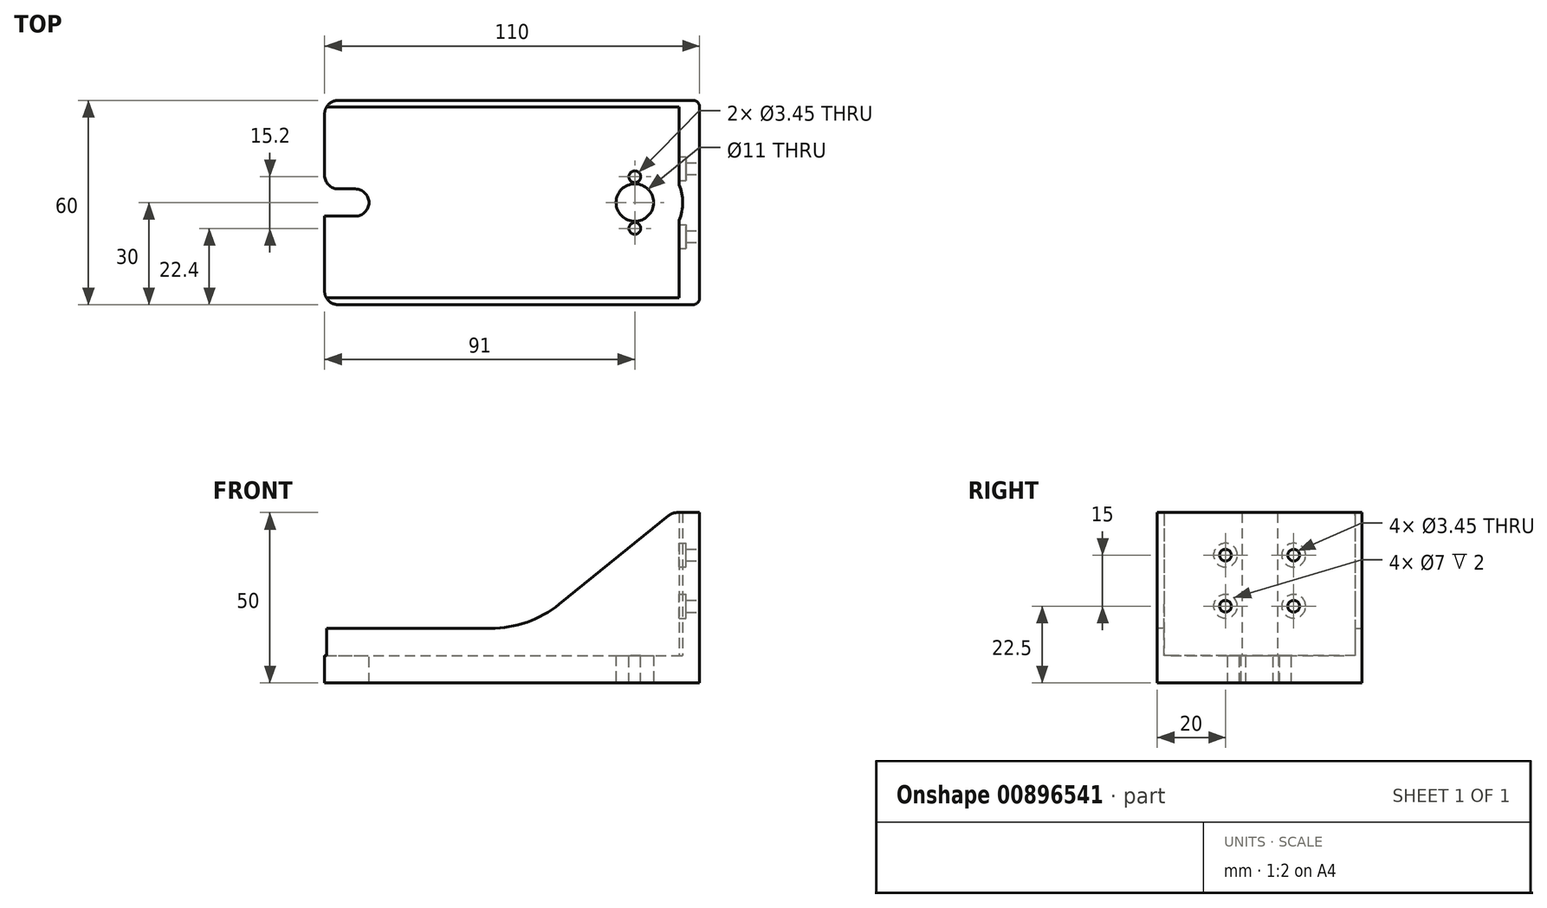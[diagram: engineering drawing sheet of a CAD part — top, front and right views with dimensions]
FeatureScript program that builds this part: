
annotation { "Feature Type Name" : "Feature", "Feature Type Description" : "" }
export const myFeature = defineFeature(function(context is Context, id is Id, definition is map)
    precondition{}
    {
        {
            var Q0;
            Q0=qCreatedBy(makeId("Top.planeOp"),FACE);
            var sketch = newSketch(context, id + "F0", { "sketchPlane" : qUnion([Q0])});
            skLineSegment(sketch, "E0.bottom", {"start": v(0, 0) * mm, "end": v(110, 0) * mm});
            skLineSegment(sketch, "E0.top", {"start": v(0, 60) * mm, "end": v(110, 60) * mm});
            skLineSegment(sketch, "E0.left", {"start": v(0, 0) * mm, "end": v(0, 60) * mm});
            skLineSegment(sketch, "E0.right", {"start": v(110, 0) * mm, "end": v(110, 60) * mm});
            skSolve(sketch);
        }
        {
            var Q0;
            Q0 = qSketchRegion(id + "F0", true);
            extrude(context, id + "F1", {"entities" : qUnion([Q0]), "depth" : 8 * mm, "offsetDistance" : 25 * mm});
        }
        {
            var Q0;
            Q0=makeQuery(id+"F1.opExtrude","SWEPT_FACE",FACE,{"disambiguationData":[OSD([sQuery(id+"F0.wireOp",EDGE,"E0.bottom")])]});
            var sketch = newSketch(context, id + "F2", { "sketchPlane" : qUnion([Q0])});
            skLineSegment(sketch, "E1", {"start": v(110, 8) * mm, "end": v(110, 50) * mm});
            skLineSegment(sketch, "E2", {"start": v(110, 50) * mm, "end": v(102, 50) * mm});
            skLineSegment(sketch, "E3", {"start": v(102, 50) * mm, "end": v(60, 16) * mm});
            skLineSegment(sketch, "E4", {"start": v(60, 16) * mm, "end": v(0, 16) * mm});
            skLineSegment(sketch, "E5", {"start": v(0, 16) * mm, "end": v(0, 8) * mm});
            skLineSegment(sketch, "E6", {"start": v(0, 8) * mm, "end": v(110, 8) * mm});
            skSolve(sketch);
        }
        {
            var Q0;
            Q0 = qSketchRegion(id + "F2", true);
            extrude(context, id + "F3", {"entities" : qUnion([Q0]), "operationType" : NewBodyOperationType.ADD, "oppositeDirection" : true, "depth" : 2 * mm, "offsetDistance" : 25 * mm});
        }
        {
            var Q0;
            Q0=makeQuery(id+"F1.opExtrude","SWEPT_FACE",FACE,{"disambiguationData":[OSD([sQuery(id+"F0.wireOp",EDGE,"E0.top")])]});
            var sketch = newSketch(context, id + "F4", { "sketchPlane" : qUnion([Q0])});
            skLineSegment(sketch, "E7", {"start": v(-110, 8) * mm, "end": v(-110, 50) * mm});
            skLineSegment(sketch, "E8", {"start": v(-110, 50) * mm, "end": v(-102, 50) * mm});
            skLineSegment(sketch, "E9", {"start": v(-102, 50) * mm, "end": v(-60, 16) * mm});
            skLineSegment(sketch, "E10", {"start": v(-60, 16) * mm, "end": v(0, 16) * mm});
            skLineSegment(sketch, "E11", {"start": v(0, 16) * mm, "end": v(0, 8) * mm});
            skLineSegment(sketch, "E12", {"start": v(0, 8) * mm, "end": v(-110, 8) * mm});
            skSolve(sketch);
        }
        {
            var Q0;
            Q0 = qSketchRegion(id + "F4", true);
            extrude(context, id + "F5", {"entities" : qUnion([Q0]), "operationType" : NewBodyOperationType.ADD, "oppositeDirection" : true, "depth" : 2 * mm, "offsetDistance" : 25 * mm});
        }
        {
            var Q0;
            Q0=makeQuery(id+"F1.opExtrude","CAP_FACE",FACE,{"disambiguationData":[OSD([sQuery(id+"F0.wireOp",EDGE,"E0.bottom"),sQuery(id+"F0.wireOp",EDGE,"E0.top"),sQuery(id+"F0.wireOp",EDGE,"E0.left"),sQuery(id+"F0.wireOp",EDGE,"E0.right")])],"isStart":false});
            var sketch = newSketch(context, id + "F6", { "sketchPlane" : qUnion([Q0])});
            skLineSegment(sketch, "E13.bottom", {"start": v(110, 58) * mm, "end": v(104, 58) * mm});
            skLineSegment(sketch, "E13.top", {"start": v(110, 2) * mm, "end": v(104, 2) * mm});
            skLineSegment(sketch, "E13.left", {"start": v(110, 58) * mm, "end": v(110, 2) * mm});
            skLineSegment(sketch, "E13.right", {"start": v(104, 58) * mm, "end": v(104, 2) * mm});
            skSolve(sketch);
        }
        {
            var Q0;
            Q0 = qSketchRegion(id + "F6", true);
            extrude(context, id + "F7", {"entities" : qUnion([Q0]), "operationType" : NewBodyOperationType.ADD, "depth" : 42 * mm, "offsetDistance" : 25 * mm});
        }
        {
            var Q0;
            Q0=makeQuery(id+"F1.opExtrude","CAP_FACE",FACE,{"disambiguationData":[OSD([sQuery(id+"F0.wireOp",EDGE,"E0.bottom"),sQuery(id+"F0.wireOp",EDGE,"E0.top"),sQuery(id+"F0.wireOp",EDGE,"E0.left"),sQuery(id+"F0.wireOp",EDGE,"E0.right")])],"isStart":false});
            var sketch = newSketch(context, id + "F8", { "sketchPlane" : qUnion([Q0])});
            skLineSegment(sketch, "E14.bottom", {"start": v(0, 34) * mm, "end": v(13, 34) * mm});
            skLineSegment(sketch, "E14.top", {"start": v(0, 26) * mm, "end": v(13, 26) * mm});
            skLineSegment(sketch, "E14.left", {"start": v(0, 34) * mm, "end": v(0, 26) * mm});
            skLineSegment(sketch, "E14.right", {"start": v(13, 34) * mm, "end": v(13, 26) * mm});
            skLineSegment(sketch, "E15", {"start": v(0, 30) * mm, "end": v(13, 30) * mm, "construction": true});
            skSolve(sketch);
        }
        {
            var Q0;
            Q0 = qSketchRegion(id + "F8", true);
            extrude(context, id + "F9", {"entities" : qUnion([Q0]), "operationType" : NewBodyOperationType.REMOVE, "oppositeDirection" : true, "depth" : 8 * mm, "offsetDistance" : 25 * mm});
        }
        {
            var Q0;
            Q0=makeQuery(id+"F5.opExtrude","SWEPT_EDGE",EDGE,{"disambiguationData":[OSD([sQuery(id+"F4.wireOp",EDGE,"E8"),sQuery(id+"F4.wireOp",EDGE,"E9")])]});
            var Q1;
            Q1=makeQuery(id+"F3.opExtrude","SWEPT_EDGE",EDGE,{"disambiguationData":[OSD([sQuery(id+"F2.wireOp",EDGE,"E2"),sQuery(id+"F2.wireOp",EDGE,"E3")])]});
            var Q2;
            Q2=makeQuery(id+"F5.boolean.opBoolean","MERGE",EDGE,{"derivedFrom":[makeQuery(id+"F1.opExtrude","SWEPT_EDGE",EDGE,{"disambiguationData":[OSD([sQuery(id+"F0.wireOp",EDGE,"E0.top"),sQuery(id+"F0.wireOp",EDGE,"E0.left")])]}),makeQuery(id+"F5.opExtrude","CAP_EDGE",EDGE,{"disambiguationData":[OSD([sQuery(id+"F4.wireOp",EDGE,"E11")])],"isStart":true})]});
            var Q3;
            Q3=makeQuery(id+"F9.boolean.opBoolean","COPY",EDGE,{"derivedFrom":makeQuery(id+"F9.opExtrude","SWEPT_EDGE",EDGE,{"disambiguationData":[OSD([sQuery(id+"F0.wireOp",EDGE,"E0.left"),sQuery(id+"F8.wireOp",EDGE,"E14.bottom"),sQuery(id+"F8.wireOp",EDGE,"E14.left")])]})});
            var Q4;
            Q4=makeQuery(id+"F9.boolean.opBoolean","COPY",EDGE,{"derivedFrom":makeQuery(id+"F9.opExtrude","SWEPT_EDGE",EDGE,{"disambiguationData":[OSD([sQuery(id+"F0.wireOp",EDGE,"E0.left"),sQuery(id+"F8.wireOp",EDGE,"E14.top"),sQuery(id+"F8.wireOp",EDGE,"E14.left")])]})});
            var Q5;
            Q5=makeQuery(id+"F9.boolean.opBoolean","COPY",EDGE,{"derivedFrom":makeQuery(id+"F9.opExtrude","SWEPT_EDGE",EDGE,{"disambiguationData":[OSD([sQuery(id+"F8.wireOp",EDGE,"E14.top"),sQuery(id+"F8.wireOp",EDGE,"E14.right")])]})});
            var Q6;
            Q6=makeQuery(id+"F9.boolean.opBoolean","COPY",EDGE,{"derivedFrom":makeQuery(id+"F9.opExtrude","SWEPT_EDGE",EDGE,{"disambiguationData":[OSD([sQuery(id+"F8.wireOp",EDGE,"E14.bottom"),sQuery(id+"F8.wireOp",EDGE,"E14.right")])]})});
            var Q7;
            Q7=makeQuery(id+"F3.boolean.opBoolean","MERGE",EDGE,{"derivedFrom":[makeQuery(id+"F1.opExtrude","SWEPT_EDGE",EDGE,{"disambiguationData":[OSD([sQuery(id+"F0.wireOp",EDGE,"E0.bottom"),sQuery(id+"F0.wireOp",EDGE,"E0.left")])]}),makeQuery(id+"F3.opExtrude","CAP_EDGE",EDGE,{"disambiguationData":[OSD([sQuery(id+"F2.wireOp",EDGE,"E5")])],"isStart":true})]});
            fillet(context, id + "F10", {"entities" : qUnion([Q0, Q1, Q2, Q3, Q4, Q5, Q6, Q7]), "radius" : 4 * mm, "tangentPropagation" : true, "defaultsChanged" : false, "vertexSettings" : [], "allowEdgeOverflow" : false});
        }
        {
            var Q0;
            Q0=makeQuery(id+"F5.opExtrude","CAP_EDGE",EDGE,{"disambiguationData":[OSD([sQuery(id+"F4.wireOp",EDGE,"E12")])],"isStart":false});
            var Q1;
            Q1=makeQuery(id+"F3.opExtrude","CAP_EDGE",EDGE,{"disambiguationData":[OSD([sQuery(id+"F2.wireOp",EDGE,"E6")])],"isStart":false});
            var Q2;
            Q2=makeQuery(id+"F3.opExtrude","SWEPT_EDGE",EDGE,{"disambiguationData":[OSD([sQuery(id+"F2.wireOp",EDGE,"E2"),sQuery(id+"F2.wireOp",EDGE,"E3")])]});
            var Q3;
            Q3=makeQuery(id+"F5.opExtrude","SWEPT_EDGE",EDGE,{"disambiguationData":[OSD([sQuery(id+"F4.wireOp",EDGE,"E8"),sQuery(id+"F4.wireOp",EDGE,"E9")])]});
            var Q4;
            Q4=makeQuery(id+"F3.boolean.opBoolean","MERGE",EDGE,{"derivedFrom":[makeQuery(id+"F1.opExtrude","SWEPT_EDGE",EDGE,{"disambiguationData":[OSD([sQuery(id+"F0.wireOp",EDGE,"E0.bottom"),sQuery(id+"F0.wireOp",EDGE,"E0.right")])]}),makeQuery(id+"F3.opExtrude","CAP_EDGE",EDGE,{"disambiguationData":[OSD([sQuery(id+"F2.wireOp",EDGE,"E1")])],"isStart":true})]});
            var Q5;
            Q5=makeQuery(id+"F5.boolean.opBoolean","MERGE",EDGE,{"derivedFrom":[makeQuery(id+"F1.opExtrude","SWEPT_EDGE",EDGE,{"disambiguationData":[OSD([sQuery(id+"F0.wireOp",EDGE,"E0.top"),sQuery(id+"F0.wireOp",EDGE,"E0.right")])]}),makeQuery(id+"F5.opExtrude","CAP_EDGE",EDGE,{"disambiguationData":[OSD([sQuery(id+"F4.wireOp",EDGE,"E7")])],"isStart":true})]});
            var Q6;
            Q6=makeQuery(id+"F7.opExtrude","SWEPT_EDGE",EDGE,{"disambiguationData":[OSD([sQuery(id+"F2.wireOp",EDGE,"E6"),sQuery(id+"F6.wireOp",EDGE,"E13.top"),sQuery(id+"F6.wireOp",EDGE,"E13.right")])]});
            var Q7;
            Q7=makeQuery(id+"F7.opExtrude","SWEPT_EDGE",EDGE,{"disambiguationData":[OSD([sQuery(id+"F4.wireOp",EDGE,"E12"),sQuery(id+"F6.wireOp",EDGE,"E13.bottom"),sQuery(id+"F6.wireOp",EDGE,"E13.right")])]});
            var Q8;
            Q8=makeQuery(id+"F7.opExtrude","CAP_EDGE",EDGE,{"disambiguationData":[OSD([sQuery(id+"F6.wireOp",EDGE,"E13.right")])],"isStart":true});
            fillet(context, id + "F11", {"entities" : qUnion([Q0, Q1, Q2, Q3, Q4, Q5, Q6, Q7, Q8]), "radius" : 2 * mm, "tangentPropagation" : true, "defaultsChanged" : true, "vertexSettings" : [], "allowEdgeOverflow" : false});
        }
        {
            var Q0;
            Q0=makeQuery(id+"F7.boolean.opBoolean","MERGE",FACE,{"derivedFrom":[makeQuery(id+"F5.boolean.opBoolean","MERGE",FACE,{"derivedFrom":[makeQuery(id+"F3.boolean.opBoolean","MERGE",FACE,{"derivedFrom":[makeQuery(id+"F1.opExtrude","SWEPT_FACE",FACE,{"disambiguationData":[OSD([sQuery(id+"F0.wireOp",EDGE,"E0.right")])]}),makeQuery(id+"F3.opExtrude","SWEPT_FACE",FACE,{"disambiguationData":[OSD([sQuery(id+"F2.wireOp",EDGE,"E1")])]})]}),makeQuery(id+"F5.opExtrude","SWEPT_FACE",FACE,{"disambiguationData":[OSD([sQuery(id+"F4.wireOp",EDGE,"E7")])]})]}),makeQuery(id+"F7.opExtrude","SWEPT_FACE",FACE,{"disambiguationData":[OSD([sQuery(id+"F6.wireOp",EDGE,"E13.left")])]})]});
            var sketch = newSketch(context, id + "F12", { "sketchPlane" : qUnion([Q0])});
            skLineSegment(sketch, "E16", {"start": v(30, 0) * mm, "end": v(30, 30) * mm, "construction": true});
            skLineSegment(sketch, "E17.bottom", {"start": v(20, 37.5) * mm, "end": v(40, 37.5) * mm, "construction": true});
            skLineSegment(sketch, "E17.top", {"start": v(20, 22.5) * mm, "end": v(40, 22.5) * mm, "construction": true});
            skLineSegment(sketch, "E17.left", {"start": v(20, 37.5) * mm, "end": v(20, 22.5) * mm, "construction": true});
            skLineSegment(sketch, "E17.right", {"start": v(40, 37.5) * mm, "end": v(40, 22.5) * mm, "construction": true});
            skLineSegment(sketch, "E18", {"start": v(30, 30) * mm, "end": v(30, 37.5) * mm, "construction": true});
            skLineSegment(sketch, "E19", {"start": v(30, 30) * mm, "end": v(20, 30) * mm, "construction": true});
            skCircle(sketch, "E20", {"center": v(20, 37.5) * mm, "radius": 1.73 * mm});
            skCircle(sketch, "E21", {"center": v(40, 37.5) * mm, "radius": 1.73 * mm});
            skCircle(sketch, "E22", {"center": v(40, 22.5) * mm, "radius": 1.73 * mm});
            skCircle(sketch, "E23", {"center": v(20, 22.5) * mm, "radius": 1.73 * mm});
            skCircle(sketch, "E24", {"center": v(20, 22.5) * mm, "radius": 3.5 * mm});
            skCircle(sketch, "E25", {"center": v(40, 22.5) * mm, "radius": 3.5 * mm});
            skCircle(sketch, "E26", {"center": v(40, 37.5) * mm, "radius": 3.5 * mm});
            skCircle(sketch, "E27", {"center": v(20, 37.5) * mm, "radius": 3.5 * mm});
            skSolve(sketch);
        }
        {
            var Q0;
            Q0=makeQuery(id+"F12.imprint","IMPRINT",FACE,{"disambiguationData":[TD([[makeQuery(id+"F12.imprint","IMPRINT",EDGE,{"derivedFrom":sQuery(id+"F12.wireOp",EDGE,"E20")}),1.0]])]});
            var Q1;
            Q1=makeQuery(id+"F12.imprint","IMPRINT",FACE,{"disambiguationData":[TD([[makeQuery(id+"F12.imprint","IMPRINT",EDGE,{"derivedFrom":sQuery(id+"F12.wireOp",EDGE,"E22")}),1.0]])]});
            var Q2;
            Q2=makeQuery(id+"F12.imprint","IMPRINT",FACE,{"disambiguationData":[TD([[makeQuery(id+"F12.imprint","IMPRINT",EDGE,{"derivedFrom":sQuery(id+"F12.wireOp",EDGE,"E23")}),1.0]])]});
            var Q3;
            Q3=makeQuery(id+"F12.imprint","IMPRINT",FACE,{"disambiguationData":[TD([[makeQuery(id+"F12.imprint","IMPRINT",EDGE,{"derivedFrom":sQuery(id+"F12.wireOp",EDGE,"E21")}),1.0]])]});
            extrude(context, id + "F13", {"entities" : qUnion([Q0, Q1, Q2, Q3]), "operationType" : NewBodyOperationType.REMOVE, "oppositeDirection" : true, "depth" : 6 * mm, "offsetDistance" : 25 * mm});
        }
        {
            var Q0;
            Q0 = qSketchRegion(id + "F12", true);
            extrude(context, id + "F14", {"entities" : qUnion([Q0]), "oppositeDirection" : true, "depth" : 3 * mm, "offsetDistance" : 25 * mm});
        }
        {
            var Q0;
            Q0=makeQuery(id+"F14.opExtrude","SWEPT_BODY",BODY,{"disambiguationData":[OSD([sQuery(id+"F12.wireOp",EDGE,"E20"),sQuery(id+"F12.wireOp",EDGE,"E27")])]});
            var Q1;
            Q1=makeQuery(id+"F14.opExtrude","SWEPT_BODY",BODY,{"disambiguationData":[OSD([sQuery(id+"F12.wireOp",EDGE,"E21"),sQuery(id+"F12.wireOp",EDGE,"E26")])]});
            var Q2;
            Q2=makeQuery(id+"F14.opExtrude","SWEPT_BODY",BODY,{"disambiguationData":[OSD([sQuery(id+"F12.wireOp",EDGE,"E22"),sQuery(id+"F12.wireOp",EDGE,"E25")])]});
            var Q3;
            Q3=makeQuery(id+"F14.opExtrude","SWEPT_BODY",BODY,{"disambiguationData":[OSD([sQuery(id+"F12.wireOp",EDGE,"E23"),sQuery(id+"F12.wireOp",EDGE,"E24")])]});
            transform(context, id + "F15", {"entities" : qUnion([Q0, Q1, Q2, Q3]), "transformType" : TransformType.TRANSLATION_3D, "dx" : -4 * mm, "dy" : 0 * mm, "dz" : 0 * mm, "makeCopy" : false});
        }
        {
            var Q0;
            Q0=makeQuery(id+"F14.opExtrude","SWEPT_BODY",BODY,{"disambiguationData":[OSD([sQuery(id+"F12.wireOp",EDGE,"E20"),sQuery(id+"F12.wireOp",EDGE,"E27")])]});
            var Q1;
            Q1=makeQuery(id+"F14.opExtrude","SWEPT_BODY",BODY,{"disambiguationData":[OSD([sQuery(id+"F12.wireOp",EDGE,"E21"),sQuery(id+"F12.wireOp",EDGE,"E26")])]});
            var Q2;
            Q2=makeQuery(id+"F14.opExtrude","SWEPT_BODY",BODY,{"disambiguationData":[OSD([sQuery(id+"F12.wireOp",EDGE,"E22"),sQuery(id+"F12.wireOp",EDGE,"E25")])]});
            var Q3;
            Q3=makeQuery(id+"F14.opExtrude","SWEPT_BODY",BODY,{"disambiguationData":[OSD([sQuery(id+"F12.wireOp",EDGE,"E23"),sQuery(id+"F12.wireOp",EDGE,"E24")])]});
            var Q4;
            Q4=makeQuery(id+"F1.opExtrude","SWEPT_BODY",BODY,{"disambiguationData":[OSD([sQuery(id+"F0.wireOp",EDGE,"E0.bottom"),sQuery(id+"F0.wireOp",EDGE,"E0.top"),sQuery(id+"F0.wireOp",EDGE,"E0.left"),sQuery(id+"F0.wireOp",EDGE,"E0.right")])]});
            booleanBodies(context, id + "F16", {"operationType" : BooleanOperationType.SUBTRACTION, "tools" : qUnion([Q0, Q1, Q2, Q3]), "targets" : qUnion([Q4])});
        }
        {
            var Q0;
            Q0=makeQuery(id+"F1.opExtrude","CAP_FACE",FACE,{"disambiguationData":[OSD([sQuery(id+"F0.wireOp",EDGE,"E0.bottom"),sQuery(id+"F0.wireOp",EDGE,"E0.top"),sQuery(id+"F0.wireOp",EDGE,"E0.left"),sQuery(id+"F0.wireOp",EDGE,"E0.right")])],"isStart":true});
            var sketch = newSketch(context, id + "F17", { "sketchPlane" : qUnion([Q0])});
            skLineSegment(sketch, "E28", {"start": v(110, -30) * mm, "end": v(91, -30) * mm, "construction": true});
            skCircle(sketch, "E29", {"center": v(91, -30) * mm, "radius": 5.5 * mm});
            skSolve(sketch);
        }
        {
            var Q0;
            Q0 = qSketchRegion(id + "F17", true);
            extrude(context, id + "F18", {"entities" : qUnion([Q0]), "operationType" : NewBodyOperationType.REMOVE, "oppositeDirection" : true, "depth" : 8 * mm, "offsetDistance" : 25 * mm});
        }
        {
            var Q0;
            Q0=makeQuery(id+"F1.opExtrude","CAP_FACE",FACE,{"disambiguationData":[OSD([sQuery(id+"F0.wireOp",EDGE,"E0.bottom"),sQuery(id+"F0.wireOp",EDGE,"E0.top"),sQuery(id+"F0.wireOp",EDGE,"E0.left"),sQuery(id+"F0.wireOp",EDGE,"E0.right")])],"isStart":false});
            var sketch = newSketch(context, id + "F19", { "sketchPlane" : qUnion([Q0])});
            skCircle(sketch, "E30", {"center": v(91, 30) * mm, "radius": 14 * mm});
            skCircle(sketch, "E31", {"center": v(91, 30) * mm, "radius": 7.6 * mm, "construction": true});
            skLineSegment(sketch, "E32", {"start": v(91, 30) * mm, "end": v(83.4, 30) * mm, "construction": true});
            skCircle(sketch, "E33", {"center": v(83.4, 30) * mm, "radius": 1.73 * mm});
            skCircle(sketch, "E34.1.0", {"center": v(-18, 77.4) * mm, "radius": 1.73 * mm});
            skLineSegment(sketch, "E34.1.1", {"start": v(-18, 85) * mm, "end": v(-18, 77.4) * mm, "construction": true});
            skCircle(sketch, "E34.2.0", {"center": v(-77.4, -18) * mm, "radius": 1.73 * mm});
            skLineSegment(sketch, "E34.2.1", {"start": v(-85, -18) * mm, "end": v(-77.4, -18) * mm, "construction": true});
            skPoint(sketch, "E34.center", {"position": v(0, 0) * mm});
            skCircle(sketch, "E35.1.3.0", {"center": v(18, -77.4) * mm, "radius": 1.73 * mm});
            skLineSegment(sketch, "E35.2.3.0", {"start": v(18, -85) * mm, "end": v(18, -77.4) * mm, "construction": true});
            skCircle(sketch, "E36.1.1", {"center": v(91, 22.4) * mm, "radius": 1.73 * mm});
            skCircle(sketch, "E36.2.1", {"center": v(98.6, 30) * mm, "radius": 1.73 * mm});
            skCircle(sketch, "E37.2.3.0", {"center": v(91, 37.6) * mm, "radius": 1.73 * mm});
            skSolve(sketch);
        }
        {
            var Q0;
            Q0=makeQuery(id+"F19.imprint","IMPRINT",FACE,{"disambiguationData":[TD([[makeQuery(id+"F19.imprint","IMPRINT",EDGE,{"derivedFrom":sQuery(id+"F19.wireOp",EDGE,"E37.2.3.0")}),1.0]])]});
            var Q1;
            Q1=makeQuery(id+"F19.imprint","IMPRINT",FACE,{"disambiguationData":[TD([[makeQuery(id+"F19.imprint","IMPRINT",EDGE,{"derivedFrom":sQuery(id+"F19.wireOp",EDGE,"E36.1.1")}),1.0]])]});
            extrude(context, id + "F20", {"entities" : qUnion([Q0, Q1]), "operationType" : NewBodyOperationType.REMOVE, "oppositeDirection" : true, "depth" : 8 * mm, "offsetDistance" : 25 * mm});
        }
        {
            var Q0;
            Q0 = qSketchRegion(id + "F19", true);
            var Q1;
            Q1=makeQuery(id+"F19.imprint","IMPRINT",FACE,{"disambiguationData":[TD([[makeQuery(id+"F19.imprint","IMPRINT",EDGE,{"derivedFrom":sQuery(id+"F19.wireOp",EDGE,"E36.2.1")}),1.0]])]});
            extrude(context, id + "F21", {"entities" : qUnion([Q0, Q1]), "operationType" : NewBodyOperationType.REMOVE, "depth" : 55 * mm, "offsetDistance" : 25 * mm});
        }
        {
            var Q0;
            Q0=makeQuery(id+"F5.opExtrude","SWEPT_EDGE",EDGE,{"disambiguationData":[OSD([sQuery(id+"F4.wireOp",EDGE,"E9"),sQuery(id+"F4.wireOp",EDGE,"E10")])]});
            var Q1;
            Q1=makeQuery(id+"F3.opExtrude","SWEPT_EDGE",EDGE,{"disambiguationData":[OSD([sQuery(id+"F2.wireOp",EDGE,"E3"),sQuery(id+"F2.wireOp",EDGE,"E4")])]});
            fillet(context, id + "F22", {"entities" : qUnion([Q0, Q1]), "tangentPropagation" : true, "radius" : 32 * mm, "defaultsChanged" : true, "vertexSettings" : [], "allowEdgeOverflow" : false});
        }
    });
